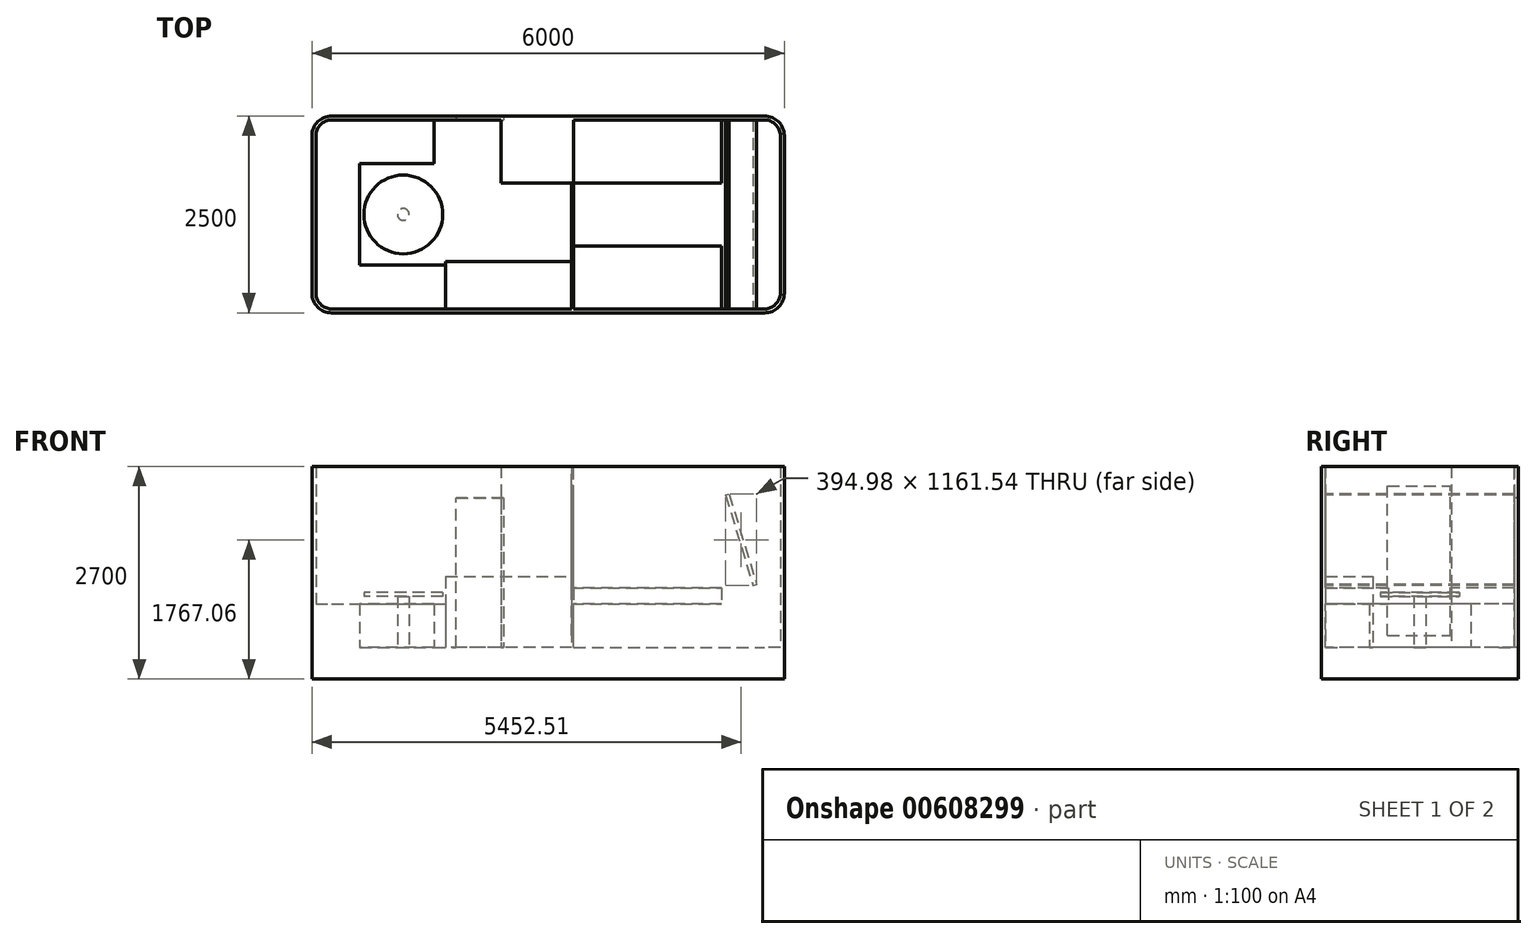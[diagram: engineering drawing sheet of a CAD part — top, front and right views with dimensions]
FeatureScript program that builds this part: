
annotation { "Feature Type Name" : "Feature", "Feature Type Description" : "" }
export const myFeature = defineFeature(function(context is Context, id is Id, definition is map)
    precondition{}
    {
        {
            var Q0;
            Q0=qCreatedBy(makeId("Top.planeOp"),FACE);
            var sketch = newSketch(context, id + "F0", { "sketchPlane" : qUnion([Q0])});
            skLineSegment(sketch, "E0.bottom", {"start": v(-5382.04, 2423.5) * mm, "end": v(117.96, 2423.5) * mm});
            skLineSegment(sketch, "E0.top", {"start": v(-5382.04, -76.5) * mm, "end": v(117.96, -76.5) * mm});
            skLineSegment(sketch, "E0.left", {"start": v(-5632.04, 2173.5) * mm, "end": v(-5632.04, 173.5) * mm});
            skLineSegment(sketch, "E0.right", {"start": v(367.96, 2173.5) * mm, "end": v(367.96, 173.5) * mm});
            skPoint(sketch, "E1.visualSharp", {"position": v(367.96, 2423.5) * mm});
            skArc(sketch, "E1.filletArc", {"start": v(367.96, 2173.5) * mm, "mid": v(294.73, 2350.28) * mm, "end": v(117.96, 2423.5) * mm});
            skPoint(sketch, "E2.visualSharp", {"position": v(367.96, -76.5) * mm});
            skArc(sketch, "E2.filletArc", {"start": v(117.96, -76.5) * mm, "mid": v(294.73, -3.28) * mm, "end": v(367.96, 173.5) * mm});
            skPoint(sketch, "E3.visualSharp", {"position": v(-5632.04, -76.5) * mm});
            skArc(sketch, "E3.filletArc", {"start": v(-5632.04, 173.5) * mm, "mid": v(-5558.82, -3.28) * mm, "end": v(-5382.04, -76.5) * mm});
            skPoint(sketch, "E4.visualSharp", {"position": v(-5632.04, 2423.5) * mm});
            skArc(sketch, "E4.filletArc", {"start": v(-5382.04, 2423.5) * mm, "mid": v(-5558.82, 2350.28) * mm, "end": v(-5632.04, 2173.5) * mm});
            skArc(sketch, "E5.0", {"start": v(-5582.04, 173.5) * mm, "mid": v(-5523.46, 32.08) * mm, "end": v(-5382.04, -26.5) * mm});
            skLineSegment(sketch, "E5.1", {"start": v(-5582.04, 2173.5) * mm, "end": v(-5582.04, 173.5) * mm});
            skLineSegment(sketch, "E5.2", {"start": v(-5382.04, -26.5) * mm, "end": v(117.96, -26.5) * mm});
            skArc(sketch, "E5.3", {"start": v(-5382.04, 2373.5) * mm, "mid": v(-5523.46, 2314.92) * mm, "end": v(-5582.04, 2173.5) * mm});
            skArc(sketch, "E5.4", {"start": v(117.96, -26.5) * mm, "mid": v(259.38, 32.08) * mm, "end": v(317.96, 173.5) * mm});
            skLineSegment(sketch, "E5.5", {"start": v(317.96, 2173.5) * mm, "end": v(317.96, 173.5) * mm});
            skArc(sketch, "E5.6", {"start": v(317.96, 2173.5) * mm, "mid": v(259.38, 2314.92) * mm, "end": v(117.96, 2373.5) * mm});
            skLineSegment(sketch, "E5.7", {"start": v(-5382.04, 2373.5) * mm, "end": v(117.96, 2373.5) * mm});
            skSolve(sketch);
        }
        {
            var Q0;
            Q0=makeQuery(id+"F0.imprint","IMPRINT",FACE,{"disambiguationData":[TD([[makeQuery(id+"F0.imprint","IMPRINT",EDGE,{"derivedFrom":sQuery(id+"F0.wireOp",EDGE,"E0.bottom")}),-1.0]])]});
            extrude(context, id + "F1", {"entities" : qUnion([Q0]), "depth" : 2700 * mm, "offsetDistance" : 25 * mm});
        }
        {
            var Q0;
            Q0=makeQuery(id+"F1.opExtrude","CAP_FACE",FACE,{"disambiguationData":[OSD([sQuery(id+"F0.wireOp",EDGE,"E0.bottom"),sQuery(id+"F0.wireOp",EDGE,"E0.top"),sQuery(id+"F0.wireOp",EDGE,"E0.left"),sQuery(id+"F0.wireOp",EDGE,"E0.right"),sQuery(id+"F0.wireOp",EDGE,"E1.filletArc"),sQuery(id+"F0.wireOp",EDGE,"E2.filletArc"),sQuery(id+"F0.wireOp",EDGE,"E3.filletArc"),sQuery(id+"F0.wireOp",EDGE,"E4.filletArc"),sQuery(id+"F0.wireOp",EDGE,"E5.0"),sQuery(id+"F0.wireOp",EDGE,"E5.1"),sQuery(id+"F0.wireOp",EDGE,"E5.2"),sQuery(id+"F0.wireOp",EDGE,"E5.3"),sQuery(id+"F0.wireOp",EDGE,"E5.4"),sQuery(id+"F0.wireOp",EDGE,"E5.5"),sQuery(id+"F0.wireOp",EDGE,"E5.6"),sQuery(id+"F0.wireOp",EDGE,"E5.7")])],"isStart":true});
            var sketch = newSketch(context, id + "F2", { "sketchPlane" : qUnion([Q0])});
            skSolve(sketch);
        }
        {
            var Q0;
            Q0=makeQuery(id+"F2.imprint","IMPRINT",FACE,{"disambiguationData":[TD([[makeQuery(id+"F2.imprint","IMPRINT",EDGE,{"derivedFrom":makeQuery(id+"F1.opExtrude","CAP_EDGE",EDGE,{"disambiguationData":[OSD([sQuery(id+"F0.wireOp",EDGE,"E5.0")])],"isStart":true})}),-1.0]])]});
            extrude(context, id + "F3", {"entities" : qUnion([Q0]), "operationType" : NewBodyOperationType.ADD, "oppositeDirection" : true, "depth" : 400 * mm, "offsetDistance" : 25 * mm});
        }
        {
            var Q0;
            Q0=makeQuery(id+"F3.opExtrude","CAP_FACE",FACE,{"disambiguationData":[OSD([sQuery(id+"F0.wireOp",EDGE,"E5.0"),sQuery(id+"F0.wireOp",EDGE,"E5.1"),sQuery(id+"F0.wireOp",EDGE,"E5.2"),sQuery(id+"F0.wireOp",EDGE,"E5.3"),sQuery(id+"F0.wireOp",EDGE,"E5.4"),sQuery(id+"F0.wireOp",EDGE,"E5.5"),sQuery(id+"F0.wireOp",EDGE,"E5.6"),sQuery(id+"F0.wireOp",EDGE,"E5.7")])],"isStart":false});
            var sketch = newSketch(context, id + "F4", { "sketchPlane" : qUnion([Q0])});
            skLineSegment(sketch, "E6", {"start": v(-4082.04, 2373.5) * mm, "end": v(-4082.04, 1818.5) * mm});
            skLineSegment(sketch, "E7", {"start": v(-4082.04, 1818.5) * mm, "end": v(-5027.04, 1818.5) * mm});
            skLineSegment(sketch, "E8", {"start": v(-5027.04, 1818.5) * mm, "end": v(-5027.04, 528.5) * mm});
            skLineSegment(sketch, "E9", {"start": v(-5027.04, 528.5) * mm, "end": v(-3932.04, 528.5) * mm});
            skLineSegment(sketch, "E10", {"start": v(-3932.04, 528.5) * mm, "end": v(-3932.04, -26.5) * mm});
            skSolve(sketch);
        }
        {
            var Q0;
            {var subQ2=sQuery(id+"F4.wireOp",EDGE,"E6");Q0=makeQuery(id+"F4.imprint","IMPRINT",FACE,{"disambiguationData":[TD([[makeQuery(id+"F4.imprint","IMPRINT",EDGE,{"derivedFrom":subQ2}),-1.0]])]});}
            extrude(context, id + "F5", {"entities" : qUnion([Q0]), "operationType" : NewBodyOperationType.ADD, "depth" : 555 * mm, "offsetDistance" : 25 * mm});
        }
        {
            var Q0;
            Q0=makeQuery(id+"F3.opExtrude","CAP_FACE",FACE,{"disambiguationData":[OSD([sQuery(id+"F0.wireOp",EDGE,"E5.0"),sQuery(id+"F0.wireOp",EDGE,"E5.1"),sQuery(id+"F0.wireOp",EDGE,"E5.2"),sQuery(id+"F0.wireOp",EDGE,"E5.3"),sQuery(id+"F0.wireOp",EDGE,"E5.4"),sQuery(id+"F0.wireOp",EDGE,"E5.5"),sQuery(id+"F0.wireOp",EDGE,"E5.6"),sQuery(id+"F0.wireOp",EDGE,"E5.7")])],"isStart":false});
            var sketch = newSketch(context, id + "F6", { "sketchPlane" : qUnion([Q0])});
            skLineSegment(sketch, "E11.bottom", {"start": v(-2332.04, -26.5) * mm, "end": v(-3932.04, -26.5) * mm});
            skLineSegment(sketch, "E11.top", {"start": v(-2332.04, 573.5) * mm, "end": v(-3932.04, 573.5) * mm});
            skLineSegment(sketch, "E11.left", {"start": v(-2332.04, -26.5) * mm, "end": v(-2332.04, 573.5) * mm});
            skLineSegment(sketch, "E11.right", {"start": v(-3932.04, -26.5) * mm, "end": v(-3932.04, 573.5) * mm});
            skSolve(sketch);
        }
        {
            var Q0;
            {var subQ2=sQuery(id+"F6.wireOp",EDGE,"E11.bottom");Q0=makeQuery(id+"F6.imprint","IMPRINT",FACE,{"disambiguationData":[TD([[makeQuery(id+"F6.imprint","IMPRINT",EDGE,{"derivedFrom":subQ2}),1.0]])]});}
            extrude(context, id + "F7", {"entities" : qUnion([Q0]), "operationType" : NewBodyOperationType.ADD, "depth" : 900 * mm, "offsetDistance" : 25 * mm});
        }
        {
            var Q0;
            Q0=makeQuery(id+"F1.opExtrude","SWEPT_FACE",FACE,{"disambiguationData":[OSD([sQuery(id+"F0.wireOp",EDGE,"E5.2")])]});
            var sketch = newSketch(context, id + "F8", { "sketchPlane" : qUnion([Q0])});
            skLineSegment(sketch, "E12.bottom", {"start": v(377.02, 2334.1) * mm, "end": v(332.04, 2347.82) * mm});
            skLineSegment(sketch, "E12.top", {"start": v(27.02, 1186.29) * mm, "end": v(-17.96, 1200) * mm});
            skLineSegment(sketch, "E12.left", {"start": v(377.02, 2334.1) * mm, "end": v(27.02, 1186.29) * mm});
            skLineSegment(sketch, "E12.right", {"start": v(332.04, 2347.82) * mm, "end": v(-17.96, 1200) * mm});
            skSolve(sketch);
        }
        {
            var Q0;
            Q0=makeQuery(id+"F8.imprint","IMPRINT",FACE,{"disambiguationData":[TD([[makeQuery(id+"F8.imprint","IMPRINT",EDGE,{"derivedFrom":sQuery(id+"F8.wireOp",EDGE,"E12.bottom")}),1.0]])]});
            extrude(context, id + "F9", {"entities" : qUnion([Q0]), "operationType" : NewBodyOperationType.ADD, "depth" : 2400 * mm, "offsetDistance" : 25 * mm});
        }
        {
            var Q0;
            Q0=makeQuery(id+"F5.opExtrude","CAP_FACE",FACE,{"disambiguationData":[OSD([sQuery(id+"F0.wireOp",EDGE,"E5.0"),sQuery(id+"F0.wireOp",EDGE,"E5.1"),sQuery(id+"F0.wireOp",EDGE,"E5.2"),sQuery(id+"F0.wireOp",EDGE,"E5.3"),sQuery(id+"F0.wireOp",EDGE,"E5.7"),sQuery(id+"F4.wireOp",EDGE,"E6"),sQuery(id+"F4.wireOp",EDGE,"E7"),sQuery(id+"F4.wireOp",EDGE,"E8"),sQuery(id+"F4.wireOp",EDGE,"E9"),sQuery(id+"F4.wireOp",EDGE,"E10")])],"isStart":false});
            var sketch = newSketch(context, id + "F10", { "sketchPlane" : qUnion([Q0])});
            skLineSegment(sketch, "E13.bottom", {"start": v(-2332.04, -26.5) * mm, "end": v(-432.04, -26.5) * mm});
            skLineSegment(sketch, "E13.top", {"start": v(-2332.04, 773.5) * mm, "end": v(-432.04, 773.5) * mm});
            skLineSegment(sketch, "E13.left", {"start": v(-2332.04, -26.5) * mm, "end": v(-2332.04, 773.5) * mm});
            skLineSegment(sketch, "E13.right", {"start": v(-432.04, -26.5) * mm, "end": v(-432.04, 773.5) * mm});
            skLineSegment(sketch, "E14.bottom", {"start": v(-432.04, 2373.5) * mm, "end": v(-2332.04, 2373.5) * mm});
            skLineSegment(sketch, "E14.top", {"start": v(-432.04, 1573.5) * mm, "end": v(-2332.04, 1573.5) * mm});
            skLineSegment(sketch, "E14.left", {"start": v(-432.04, 2373.5) * mm, "end": v(-432.04, 1573.5) * mm});
            skLineSegment(sketch, "E14.right", {"start": v(-2332.04, 2373.5) * mm, "end": v(-2332.04, 1573.5) * mm});
            skSolve(sketch);
        }
        {
            var Q0;
            Q0=makeQuery(id+"F10.imprint","IMPRINT",FACE,{"disambiguationData":[TD([[makeQuery(id+"F10.imprint","IMPRINT",EDGE,{"derivedFrom":sQuery(id+"F10.wireOp",EDGE,"E13.bottom")}),1.0]])]});
            var Q1;
            Q1=makeQuery(id+"F10.imprint","IMPRINT",FACE,{"disambiguationData":[TD([[makeQuery(id+"F10.imprint","IMPRINT",EDGE,{"derivedFrom":sQuery(id+"F10.wireOp",EDGE,"E14.bottom")}),1.0]])]});
            extrude(context, id + "F11", {"entities" : qUnion([Q0, Q1]), "operationType" : NewBodyOperationType.ADD, "depth" : 200 * mm, "offsetDistance" : 25 * mm});
        }
        {
            var Q0;
            Q0=makeQuery(id+"F11.opExtrude","SWEPT_FACE",FACE,{"disambiguationData":[OSD([sQuery(id+"F10.wireOp",EDGE,"E14.right")])]});
            var sketch = newSketch(context, id + "F12", { "sketchPlane" : qUnion([Q0])});
            skLineSegment(sketch, "E15.bottom", {"start": v(-2373.5, 400) * mm, "end": v(26.5, 400) * mm});
            skLineSegment(sketch, "E15.top", {"start": v(-2373.5, 2700) * mm, "end": v(26.5, 2700) * mm});
            skLineSegment(sketch, "E15.left", {"start": v(-2373.5, 400) * mm, "end": v(-2373.5, 2700) * mm});
            skLineSegment(sketch, "E15.right", {"start": v(26.5, 400) * mm, "end": v(26.5, 2700) * mm});
            skLineSegment(sketch, "E16.bottom", {"start": v(-763.21, 549.33) * mm, "end": v(-1563.21, 549.33) * mm});
            skLineSegment(sketch, "E16.top", {"start": v(-763.21, 2449.33) * mm, "end": v(-1563.21, 2449.33) * mm});
            skLineSegment(sketch, "E16.left", {"start": v(-763.21, 549.33) * mm, "end": v(-763.21, 2449.33) * mm});
            skLineSegment(sketch, "E16.right", {"start": v(-1563.21, 549.33) * mm, "end": v(-1563.21, 2449.33) * mm});
            skSolve(sketch);
        }
        {
            var Q0;
            {var subQ1=sQuery(id+"F12.wireOp",EDGE,"E15.bottom");Q0=makeQuery(id+"F12.imprint","IMPRINT",FACE,{"disambiguationData":[TD([[makeQuery(id+"F12.imprint","IMPRINT",EDGE,{"derivedFrom":subQ1}),1.0]])]});}
            var Q1;
            {var subQ1=sQuery(id+"F10.wireOp",EDGE,"E14.right");var subQ2=makeQuery(id+"F11.opExtrude","CAP_EDGE",EDGE,{"disambiguationData":[OSD([subQ1])],"isStart":true});Q1=makeQuery(id+"F12.imprint","IMPRINT",FACE,{"disambiguationData":[TD([[makeQuery(id+"F12.imprint","IMPRINT",EDGE,{"derivedFrom":subQ2}),1.0]])]});}
            extrude(context, id + "F13", {"entities" : qUnion([Q0, Q1]), "operationType" : NewBodyOperationType.ADD, "oppositeDirection" : true, "depth" : 25 * mm, "offsetDistance" : 25 * mm});
        }
        {
            var Q0;
            {var subQ0=sQuery(id+"F0.wireOp",EDGE,"E5.7");var subQ4=sQuery(id+"F0.wireOp",EDGE,"E5.3");Q0=makeQuery(id+"F13.boolean.opBoolean","SPLIT",FACE,{"disambiguationData":[TD([makeQuery(id+"F1.opExtrude","SWEPT_FACE",FACE,{"disambiguationData":[OSD([subQ4])]})])],"derivedFrom":makeQuery(id+"F1.opExtrude","SWEPT_FACE",FACE,{"disambiguationData":[OSD([subQ0])]})});}
            var sketch = newSketch(context, id + "F14", { "sketchPlane" : qUnion([Q0])});
            skLineSegment(sketch, "E17.bottom", {"start": v(-3798.5, 400) * mm, "end": v(-3198.5, 400) * mm});
            skLineSegment(sketch, "E17.top", {"start": v(-3798.5, 2300) * mm, "end": v(-3198.5, 2300) * mm});
            skLineSegment(sketch, "E17.left", {"start": v(-3798.5, 400) * mm, "end": v(-3798.5, 2300) * mm});
            skLineSegment(sketch, "E17.right", {"start": v(-3198.5, 400) * mm, "end": v(-3198.5, 2300) * mm});
            skSolve(sketch);
        }
        {
            var Q0;
            Q0=makeQuery(id+"F14.imprint","IMPRINT",FACE,{"disambiguationData":[TD([[makeQuery(id+"F14.imprint","IMPRINT",EDGE,{"derivedFrom":sQuery(id+"F14.wireOp",EDGE,"E17.bottom")}),1.0]])]});
            extrude(context, id + "F15", {"entities" : qUnion([Q0]), "operationType" : NewBodyOperationType.REMOVE, "oppositeDirection" : true, "depth" : 55 * mm, "offsetDistance" : 25 * mm});
        }
        {
            var Q0;
            {var subQ0=sQuery(id+"F0.wireOp",EDGE,"E5.7");Q0=makeQuery(id+"F15.boolean.opBoolean","MERGE",FACE,{"derivedFrom":[makeQuery(id+"F13.boolean.opBoolean","SPLIT",FACE,{"disambiguationData":[TD([makeQuery(id+"F5.opExtrude","SWEPT_FACE",FACE,{"disambiguationData":[OSD([sQuery(id+"F4.wireOp",EDGE,"E6")])]})])],"derivedFrom":makeQuery(id+"F3.opExtrude","CAP_FACE",FACE,{"disambiguationData":[OSD([sQuery(id+"F0.wireOp",EDGE,"E5.0"),sQuery(id+"F0.wireOp",EDGE,"E5.1"),sQuery(id+"F0.wireOp",EDGE,"E5.2"),sQuery(id+"F0.wireOp",EDGE,"E5.3"),sQuery(id+"F0.wireOp",EDGE,"E5.4"),sQuery(id+"F0.wireOp",EDGE,"E5.5"),sQuery(id+"F0.wireOp",EDGE,"E5.6"),subQ0])],"isStart":false})})],"fromTools":[makeQuery(id+"F15.opExtrude","SWEPT_FACE",FACE,{"disambiguationData":[OSD([sQuery(id+"F14.wireOp",EDGE,"E17.bottom")])]})]});}
            var sketch = newSketch(context, id + "F16", { "sketchPlane" : qUnion([Q0])});
            skCircle(sketch, "E18", {"center": v(-4472.04, 1173.5) * mm, "radius": 75 * mm});
            skSolve(sketch);
        }
        {
            var Q0;
            Q0=makeQuery(id+"F16.imprint","IMPRINT",FACE,{"disambiguationData":[TD([[makeQuery(id+"F16.imprint","IMPRINT",EDGE,{"derivedFrom":sQuery(id+"F16.wireOp",EDGE,"E18")}),1.0]])]});
            extrude(context, id + "F17", {"entities" : qUnion([Q0]), "operationType" : NewBodyOperationType.ADD, "depth" : 650 * mm, "offsetDistance" : 25 * mm});
        }
        {
            var Q0;
            Q0=makeQuery(id+"F17.opExtrude","CAP_FACE",FACE,{"disambiguationData":[OSD([sQuery(id+"F16.wireOp",EDGE,"E18")])],"isStart":false});
            var sketch = newSketch(context, id + "F18", { "sketchPlane" : qUnion([Q0])});
            skCircle(sketch, "E19", {"center": v(-4472.04, 1173.5) * mm, "radius": 500 * mm});
            skSolve(sketch);
        }
        {
            var Q0;
            Q0=makeQuery(id+"F18.imprint","IMPRINT",FACE,{"disambiguationData":[TD([[makeQuery(id+"F18.imprint","IMPRINT",EDGE,{"derivedFrom":sQuery(id+"F18.wireOp",EDGE,"E19")}),1.0]])]});
            var Q1;
            Q1=makeQuery(id+"F18.imprint","IMPRINT",FACE,{"disambiguationData":[TD([[makeQuery(id+"F18.imprint","IMPRINT",EDGE,{"derivedFrom":makeQuery(id+"F17.opExtrude","CAP_EDGE",EDGE,{"disambiguationData":[OSD([sQuery(id+"F16.wireOp",EDGE,"E18")])],"isStart":false})}),1.0]])]});
            extrude(context, id + "F19", {"entities" : qUnion([Q0, Q1]), "depth" : 50 * mm, "offsetDistance" : 25 * mm});
        }
        {
            var Q0;
            {var subQ0=sQuery(id+"F0.wireOp",EDGE,"E5.7");Q0=makeQuery(id+"F15.boolean.opBoolean","MERGE",FACE,{"derivedFrom":[makeQuery(id+"F13.boolean.opBoolean","SPLIT",FACE,{"disambiguationData":[TD([makeQuery(id+"F5.opExtrude","SWEPT_FACE",FACE,{"disambiguationData":[OSD([sQuery(id+"F4.wireOp",EDGE,"E6")])]})])],"derivedFrom":makeQuery(id+"F3.opExtrude","CAP_FACE",FACE,{"disambiguationData":[OSD([sQuery(id+"F0.wireOp",EDGE,"E5.0"),sQuery(id+"F0.wireOp",EDGE,"E5.1"),sQuery(id+"F0.wireOp",EDGE,"E5.2"),sQuery(id+"F0.wireOp",EDGE,"E5.3"),sQuery(id+"F0.wireOp",EDGE,"E5.4"),sQuery(id+"F0.wireOp",EDGE,"E5.5"),sQuery(id+"F0.wireOp",EDGE,"E5.6"),subQ0])],"isStart":false})})],"fromTools":[makeQuery(id+"F15.opExtrude","SWEPT_FACE",FACE,{"disambiguationData":[OSD([sQuery(id+"F14.wireOp",EDGE,"E17.bottom")])]})]});}
            var sketch = newSketch(context, id + "F20", { "sketchPlane" : qUnion([Q0])});
            skLineSegment(sketch, "E20.bottom", {"start": v(-2332.04, 2373.5) * mm, "end": v(-3232.04, 2373.5) * mm});
            skLineSegment(sketch, "E20.top", {"start": v(-2332.04, 1573.5) * mm, "end": v(-3232.04, 1573.5) * mm});
            skLineSegment(sketch, "E20.left", {"start": v(-2332.04, 2373.5) * mm, "end": v(-2332.04, 1573.5) * mm});
            skLineSegment(sketch, "E20.right", {"start": v(-3232.04, 2373.5) * mm, "end": v(-3232.04, 1573.5) * mm});
            skSolve(sketch);
        }
        {
            var Q0;
            Q0=makeQuery(id+"F20.imprint","IMPRINT",FACE,{"disambiguationData":[TD([[makeQuery(id+"F20.imprint","IMPRINT",EDGE,{"derivedFrom":sQuery(id+"F20.wireOp",EDGE,"E20.top")}),-1.0]])]});
            extrude(context, id + "F21", {"entities" : qUnion([Q0]), "operationType" : NewBodyOperationType.ADD, "depth" : 2300 * mm, "offsetDistance" : 25 * mm});
        }
    });
